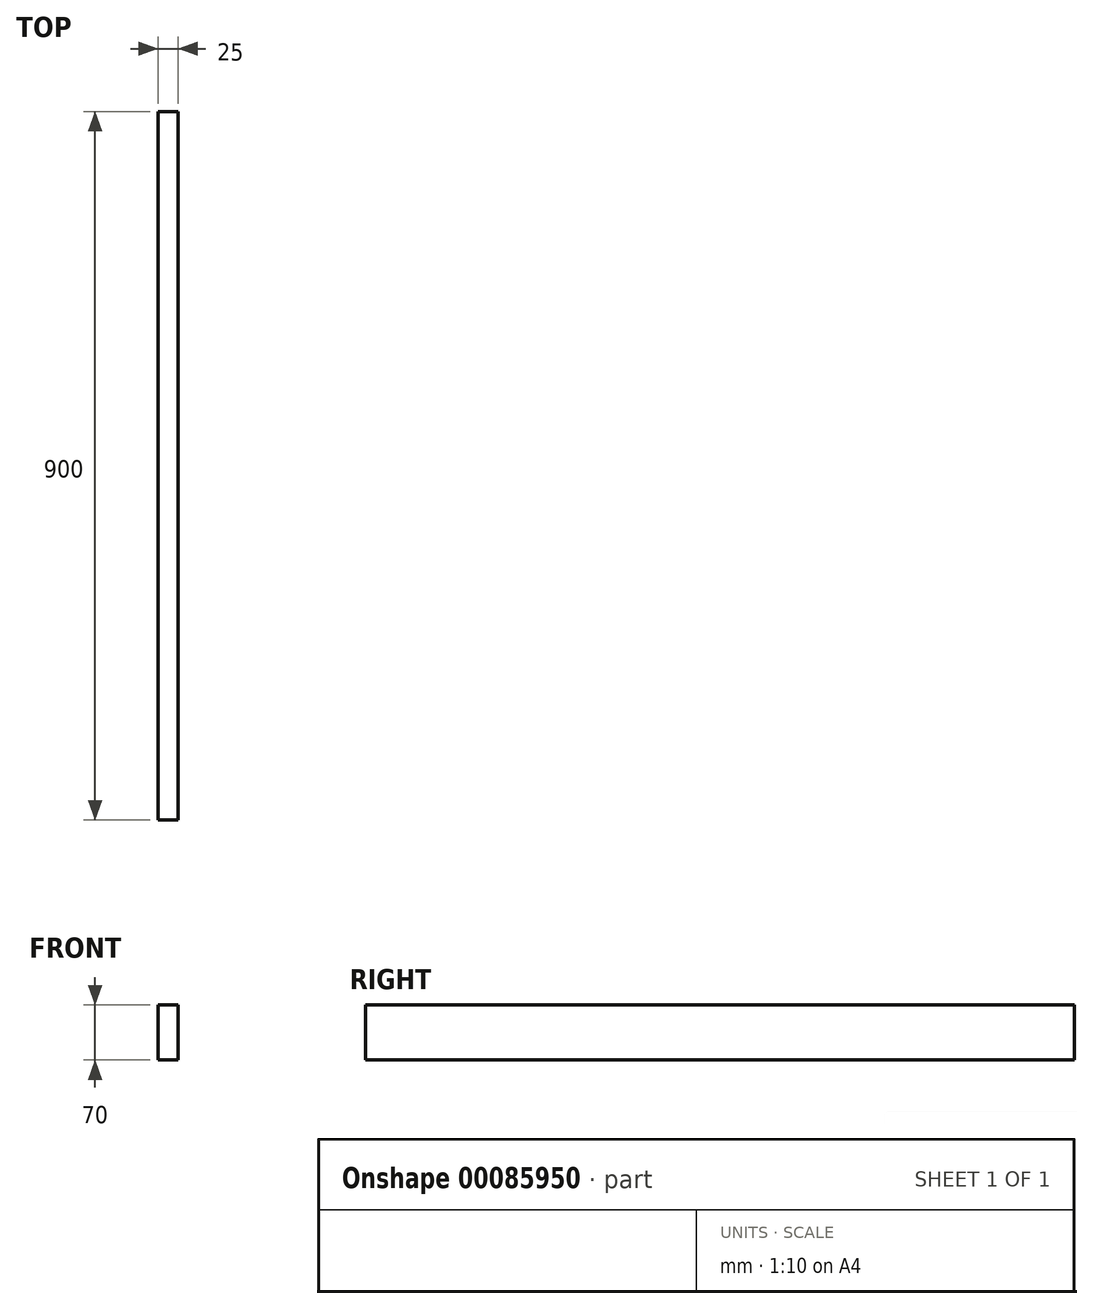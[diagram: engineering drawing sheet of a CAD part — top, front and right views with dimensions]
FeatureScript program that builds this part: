
annotation { "Feature Type Name" : "Feature", "Feature Type Description" : "" }
export const myFeature = defineFeature(function(context is Context, id is Id, definition is map)
    precondition{}
    {
        {
            var Q0;
            Q0=qCreatedBy(makeId("Right.planeOp"),FACE);
            var sketch = newSketch(context, id + "F0", { "sketchPlane" : qUnion([Q0])});
            skLineSegment(sketch, "E0.bottom", {"start": v(0, 0) * mm, "end": v(900, 0) * mm});
            skLineSegment(sketch, "E0.top", {"start": v(0, 70) * mm, "end": v(900, 70) * mm});
            skLineSegment(sketch, "E0.left", {"start": v(0, 0) * mm, "end": v(0, 70) * mm});
            skLineSegment(sketch, "E0.right", {"start": v(900, 0) * mm, "end": v(900, 70) * mm});
            skSolve(sketch);
        }
        {
            var Q0;
            Q0=makeQuery(id+"F0.imprint","IMPRINT",FACE,{"disambiguationData":[TD([[makeQuery(id+"F0.imprint","IMPRINT",EDGE,{"derivedFrom":sQuery(id+"F0.wireOp",EDGE,"E0.bottom")}),1.0]])]});
            extrude(context, id + "F1", {"entities" : qUnion([Q0]), "depth" : 25 * mm});
        }
    });
